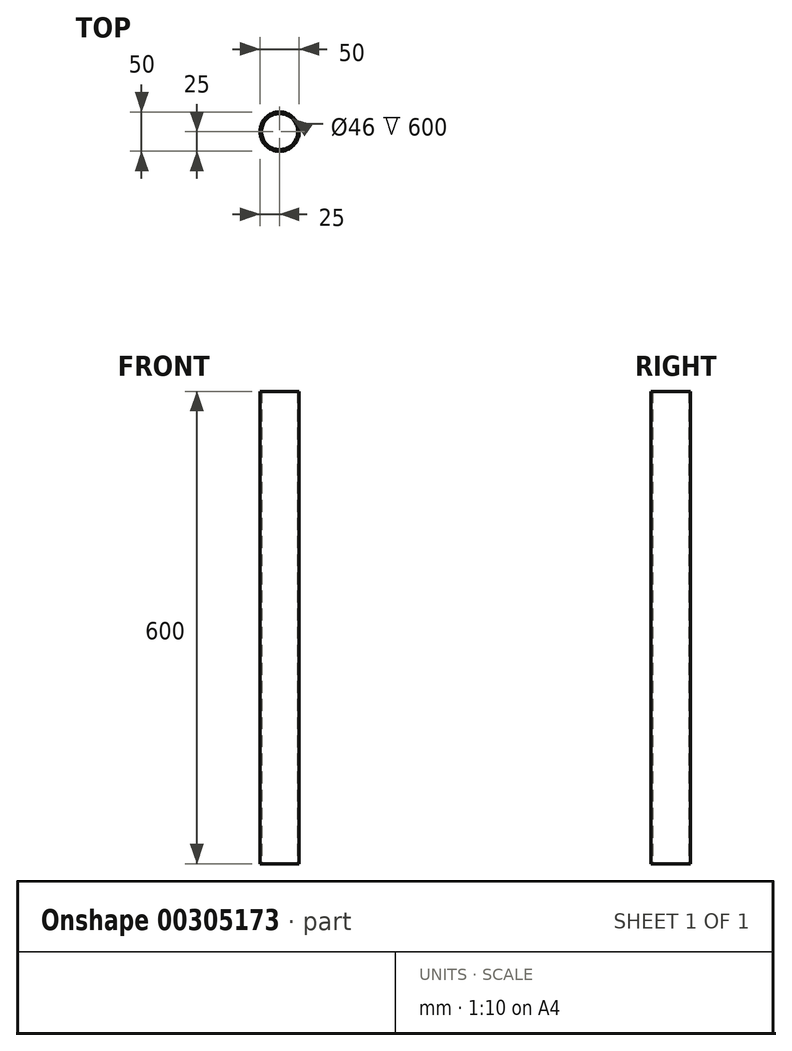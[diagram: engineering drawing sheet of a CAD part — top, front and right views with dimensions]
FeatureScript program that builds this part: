
annotation { "Feature Type Name" : "Feature", "Feature Type Description" : "" }
export const myFeature = defineFeature(function(context is Context, id is Id, definition is map)
    precondition{}
    {
        {
            var Q0;
            Q0=qCreatedBy(makeId("Top.planeOp"),FACE);
            var sketch = newSketch(context, id + "F0", { "sketchPlane" : qUnion([Q0])});
            skCircle(sketch, "E0", {"center": v(0, 0) * mm, "radius": 25 * mm});
            skCircle(sketch, "E1", {"center": v(0, 0) * mm, "radius": 23 * mm});
            skSolve(sketch);
        }
        {
            var Q0;
            Q0=makeQuery(id+"F0.imprint","IMPRINT",FACE,{"disambiguationData":[TD([[makeQuery(id+"F0.imprint","IMPRINT",EDGE,{"derivedFrom":sQuery(id+"F0.wireOp",EDGE,"E0")}),1.0]])]});
            extrude(context, id + "F1", {"entities" : qUnion([Q0]), "depth" : 600 * mm, "offsetDistance" : 25 * mm});
        }
    });
